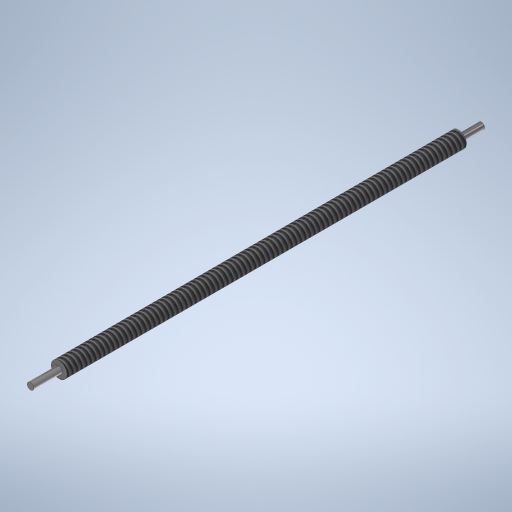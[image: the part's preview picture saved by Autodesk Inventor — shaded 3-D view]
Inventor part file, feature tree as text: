
AUTODESK INVENTOR PART (.ipt)
format: ipt  version: 2023 (Build 270158000, 158)  size: 315,392 bytes
history: native  units: mm
features: other x2, sketch x2, helix x1, thread x1
ambient origin geometry x8: Origin, YZ Plane, XZ Plane, XY Plane, X Axis, Y Axis, Z Axis, Center Point
bodies: Body1 (feature_tree)
feature tree (6):
  other  "Sólido1"
  other  "Revolução1"
  helix  "Coil1"  [1 undecoded]
  thread  "Thread2"  [1 undecoded]
  sketch  "Esboço1"  dims[d2=4.0mm]
  sketch  "Sketch3"  dims[d3=350.0mm d4=4.0mm d5=20.0mm d6=90.0deg d10=2.0mm d11=1.0mm d12=1.0mm d13=0.0mm d14=4.0mm d15=200.0mm d16=1000.0mm d17=0.0mm d18=90.0deg d19=90.0deg d20=0.0mm d21=0.0mm d22=350.0mm d23=0.0mm]
note: 2 required parameter values undecoded (feature->parameter linkage not recoverable at this tier; creation-order binding heuristic only, values carry confidence <= 0.55)
